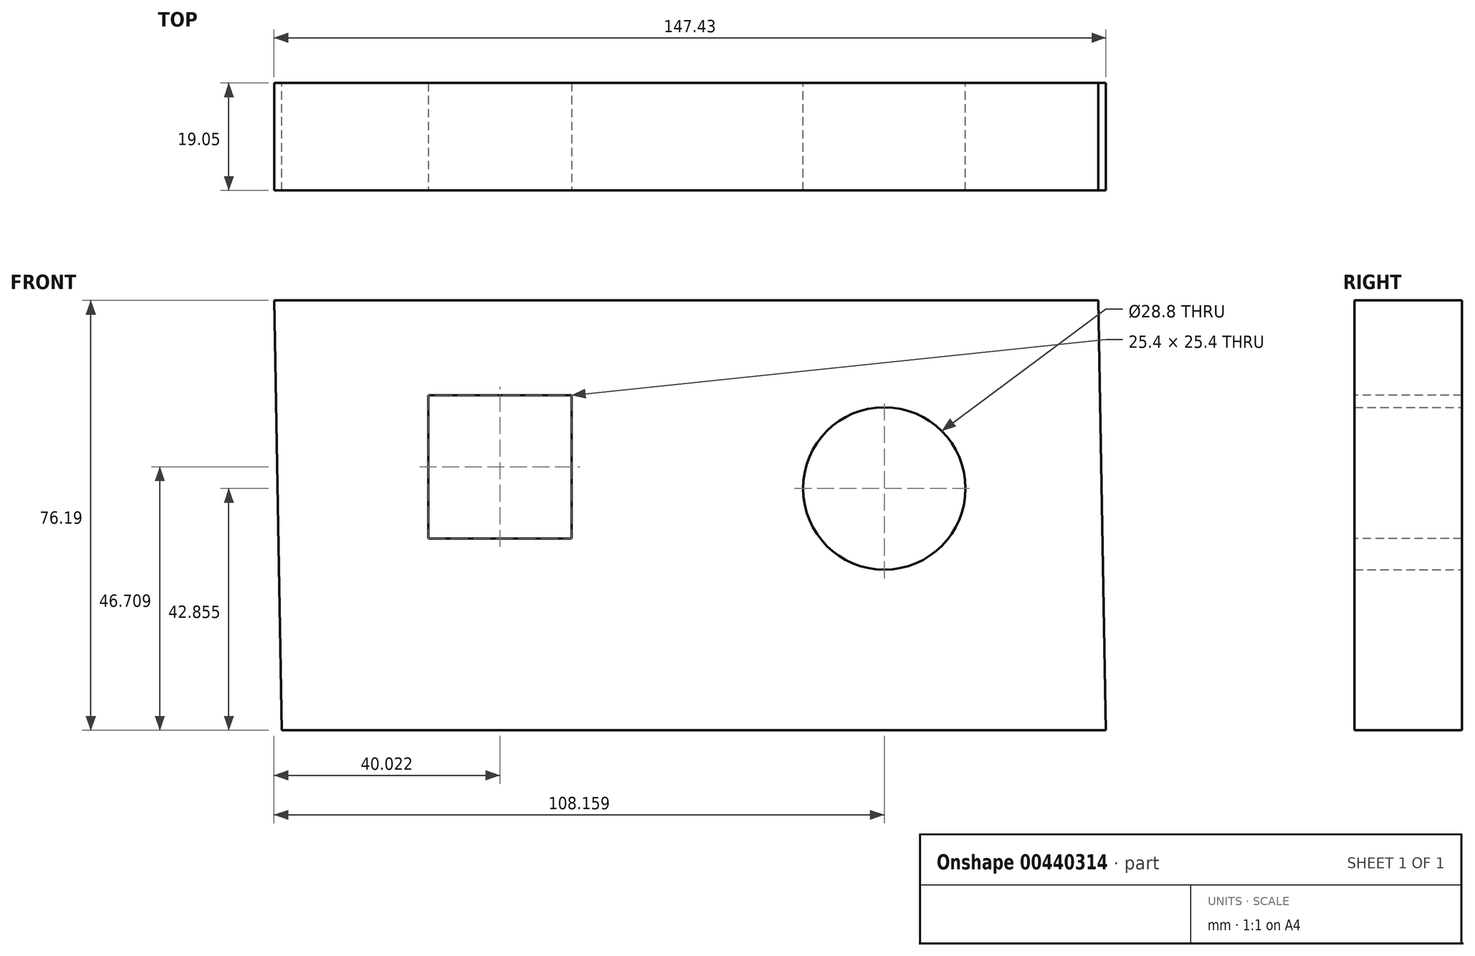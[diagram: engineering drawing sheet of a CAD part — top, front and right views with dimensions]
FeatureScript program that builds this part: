
annotation { "Feature Type Name" : "Feature", "Feature Type Description" : "" }
export const myFeature = defineFeature(function(context is Context, id is Id, definition is map)
    precondition{}
    {
        {
            var Q0;
            Q0=qCreatedBy(makeId("Front.planeOp"),FACE);
            var sketch = newSketch(context, id + "F0", { "sketchPlane" : qUnion([Q0])});
            skLineSegment(sketch, "E0", {"start": v(74.88, 76.19) * mm, "end": v(-71.17, 76.19) * mm});
            skLineSegment(sketch, "E1", {"start": v(-71.17, 76.19) * mm, "end": v(-69.79, 0) * mm});
            skLineSegment(sketch, "E2", {"start": v(-69.79, 0) * mm, "end": v(76.26, 0) * mm});
            skLineSegment(sketch, "E3", {"start": v(76.26, 0) * mm, "end": v(74.88, 76.19) * mm});
            skSolve(sketch);
        }
        {
            var Q0;
            Q0 = qSketchRegion(id + "F0", true);
            extrude(context, id + "F1", {"entities" : qUnion([Q0]), "depth" : 19.05 * mm});
        }
        {
            var Q0;
            Q0=makeQuery(id+"F1.opExtrude","CAP_FACE",FACE,{"disambiguationData":[OSD([sQuery(id+"F0.wireOp",EDGE,"E0"),sQuery(id+"F0.wireOp",EDGE,"E1"),sQuery(id+"F0.wireOp",EDGE,"E2"),sQuery(id+"F0.wireOp",EDGE,"E3")])],"isStart":false});
            var sketch = newSketch(context, id + "F2", { "sketchPlane" : qUnion([Q0])});
            skLineSegment(sketch, "E4.bottom", {"start": v(-43.85, 59.4) * mm, "end": v(-18.45, 59.4) * mm});
            skLineSegment(sketch, "E4.top", {"start": v(-43.85, 34) * mm, "end": v(-18.45, 34) * mm});
            skLineSegment(sketch, "E4.left", {"start": v(-43.85, 59.4) * mm, "end": v(-43.85, 34) * mm});
            skLineSegment(sketch, "E4.right", {"start": v(-18.45, 59.4) * mm, "end": v(-18.45, 34) * mm});
            skCircle(sketch, "E5", {"center": v(41.9, 48.36) * mm, "radius": 12.7 * mm});
            skSolve(sketch);
        }
        {
            var Q0;
            Q0=makeQuery(id+"F2.imprint","IMPRINT",FACE,{"disambiguationData":[TD([[makeQuery(id+"F2.imprint","IMPRINT",EDGE,{"derivedFrom":sQuery(id+"F2.wireOp",EDGE,"E4.bottom")}),-1.0]])]});
            extrude(context, id + "F3", {"entities" : qUnion([Q0]), "operationType" : NewBodyOperationType.REMOVE, "oppositeDirection" : true, "depth" : 25.4 * mm});
        }
        {
            var Q0;
            Q0=makeQuery(id+"F1.opExtrude","CAP_FACE",FACE,{"disambiguationData":[OSD([sQuery(id+"F0.wireOp",EDGE,"E0"),sQuery(id+"F0.wireOp",EDGE,"E1"),sQuery(id+"F0.wireOp",EDGE,"E2"),sQuery(id+"F0.wireOp",EDGE,"E3")])],"isStart":true});
            var sketch = newSketch(context, id + "F4", { "sketchPlane" : qUnion([Q0])});
            skCircle(sketch, "E6", {"center": v(-36.99, 42.86) * mm, "radius": 14.4 * mm});
            skSolve(sketch);
        }
        {
            var Q0;
            Q0 = qSketchRegion(id + "F4", true);
            var Q1;
            Q1=makeQuery(id+"F1.opExtrude","CAP_FACE",FACE,{"disambiguationData":[OSD([sQuery(id+"F0.wireOp",EDGE,"E0"),sQuery(id+"F0.wireOp",EDGE,"E1"),sQuery(id+"F0.wireOp",EDGE,"E2"),sQuery(id+"F0.wireOp",EDGE,"E3")])],"isStart":false});
            extrude(context, id + "F5", {"entities" : qUnion([Q0, Q1]), "operationType" : NewBodyOperationType.REMOVE, "oppositeDirection" : true, "depth" : 25.4 * mm});
        }
    });
